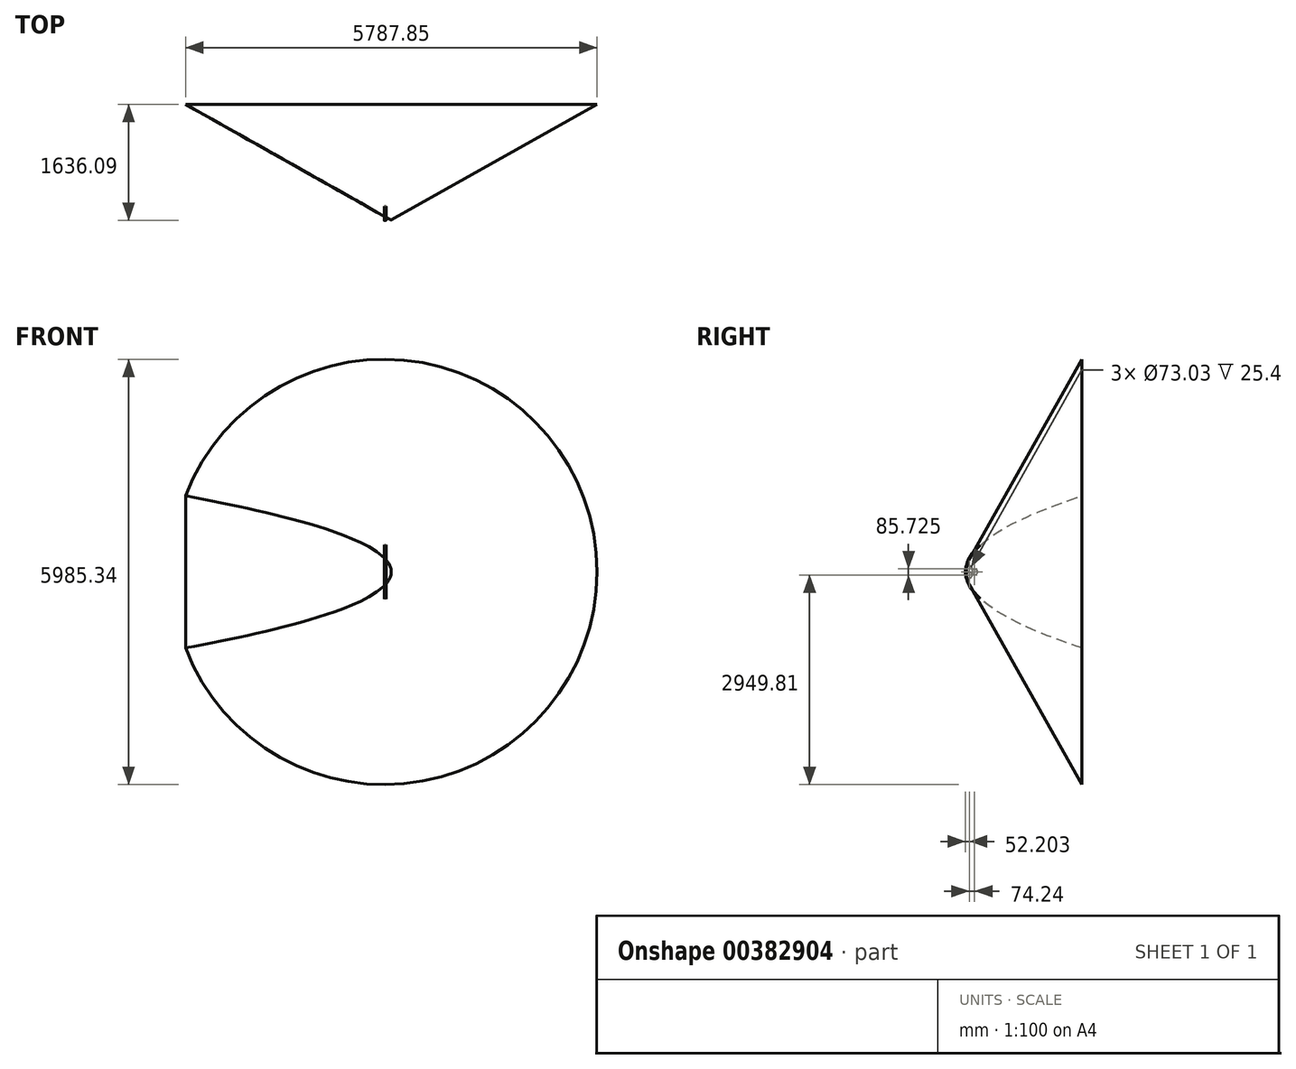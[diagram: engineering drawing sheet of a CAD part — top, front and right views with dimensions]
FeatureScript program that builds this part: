
annotation { "Feature Type Name" : "Feature", "Feature Type Description" : "" }
export const myFeature = defineFeature(function(context is Context, id is Id, definition is map)
    precondition{}
    {
        {
            var Q0;
            Q0=qCreatedBy(makeId("Top.planeOp"),FACE);
            var sketch = newSketch(context, id + "F0", { "sketchPlane" : qUnion([Q0])});
            skLineSegment(sketch, "E0", {"start": v(0, 0) * mm, "end": v(2992.67, 1685.34) * mm});
            skLineSegment(sketch, "E1", {"start": v(2992.67, 1685.34) * mm, "end": v(0, 1685.34) * mm});
            skLineSegment(sketch, "E2", {"start": v(0, 1685.34) * mm, "end": v(0, 0) * mm});
            skSolve(sketch);
        }
        {
            var Q0;
            Q0=makeQuery(id+"F0.imprint","IMPRINT",FACE,{"disambiguationData":[TD([[makeQuery(id+"F0.imprint","IMPRINT",EDGE,{"derivedFrom":sQuery(id+"F0.wireOp",EDGE,"E0")}),1.0]])]});
            var Q1;
            Q1=sQuery(id+"F0.wireOp",EDGE,"E2");
            revolve(context, id + "F1", {"entities" : qUnion([Q0]), "axis" : qUnion([Q1]), "revolveType" : RevolveType.FULL});
        }
        {
            var Q0;
            Q0=qCreatedBy(makeId("Top.planeOp"),FACE);
            var sketch = newSketch(context, id + "F2", { "sketchPlane" : qUnion([Q0])});
            skLineSegment(sketch, "E3", {"start": v(0, 0) * mm, "end": v(-231.31, 130.27) * mm, "construction": true});
            skLineSegment(sketch, "E4.0", {"start": v(398.44, -113.17) * mm, "end": v(151.52, 25.89) * mm});
            skLineSegment(sketch, "E5", {"start": v(398.44, -113.17) * mm, "end": v(601.1, -227.3) * mm});
            skLineSegment(sketch, "E6", {"start": v(601.1, -227.3) * mm, "end": v(-3246.67, -227.3) * mm});
            skLineSegment(sketch, "E7", {"start": v(-3246.67, -227.3) * mm, "end": v(-3246.67, 1939.6) * mm});
            skLineSegment(sketch, "E8", {"start": v(151.52, 25.89) * mm, "end": v(-3246.67, 1939.6) * mm});
            skLineSegment(sketch, "E9.0", {"start": v(-2992.67, 1685.34) * mm, "end": v(2992.67, 1685.34) * mm, "construction": true});
            skSolve(sketch);
        }
        {
            var Q0;
            Q0 = qSketchRegion(id + "F2", true);
            extrude(context, id + "F3", {"entities" : qUnion([Q0]), "operationType" : NewBodyOperationType.REMOVE, "endBound" : BoundingType.THROUGH_ALL, "oppositeDirection" : true, "depth" : 25.4 * mm, "hasSecondDirection" : true, "secondDirectionBound" : BoundingType.THROUGH_ALL, "secondDirectionOppositeDirection" : false, "secondDirectionDepth" : 25.4 * mm});
        }
        {
            var Q0;
            Q0=qCreatedBy(makeId("Right.planeOp"),FACE);
            var sketch = newSketch(context, id + "F4", { "sketchPlane" : qUnion([Q0])});
            skLineSegment(sketch, "E10", {"start": v(230.95, -350.68) * mm, "end": v(581.64, 0) * mm, "construction": true});
            skLineSegment(sketch, "E11", {"start": v(581.64, 0) * mm, "end": v(230.95, 350.68) * mm, "construction": true});
            skPoint(sketch, "E12", {"position": v(55.6, 0) * mm});
            skCircle(sketch, "E13", {"center": v(175.7, 0) * mm, "radius": 42.86 * mm});
            skCircle(sketch, "E14", {"center": v(101.45, 42.86) * mm, "radius": 42.86 * mm});
            skCircle(sketch, "E15", {"center": v(101.45, -42.86) * mm, "radius": 42.86 * mm});
            skLineSegment(sketch, "E16", {"start": v(230.95, -350.68) * mm, "end": v(230.95, 350.68) * mm, "construction": true});
            skPoint(sketch, "E17", {"position": v(218.56, 0) * mm});
            skLineSegment(sketch, "E18", {"start": v(55.6, 0) * mm, "end": v(55.6, -375.44) * mm, "construction": true});
            skLineSegment(sketch, "E19", {"start": v(55.6, 0) * mm, "end": v(55.6, 375.44) * mm, "construction": true});
            skLineSegment(sketch, "E20", {"start": v(55.6, -375.44) * mm, "end": v(256.58, -375.44) * mm, "construction": true});
            skLineSegment(sketch, "E21", {"start": v(55.6, 375.44) * mm, "end": v(256.58, 375.44) * mm, "construction": true});
            skFitSpline(sketch, "E22", {"points": [v(1685.34, 1069.12) * mm, v(1649.33, 1057.31) * mm, v(1577.35, 1033.3) * mm, v(1469.49, 996.05) * mm, v(1361.76, 957.39) * mm, v(1254.16, 917.16) * mm, v(1146.74, 875.15) * mm, v(1057.36, 838.44) * mm, v(985.98, 807.9) * mm, v(932.5, 784.34) * mm, v(879.08, 760.1) * mm, v(825.77, 735.1) * mm, v(772.56, 709.27) * mm, v(719.47, 682.53) * mm, v(666.5, 654.77) * mm, v(622.48, 630.67) * mm, v(587.34, 610.75) * mm, v(561.03, 595.45) * mm, v(534.77, 579.78) * mm, v(499.82, 558.35) * mm, v(456.36, 530.53) * mm, v(404.61, 495.2) * mm, v(361.9, 463.81) * mm, v(328.04, 437.27) * mm, v(302.8, 416.56) * mm, v(277.77, 394.94) * mm, v(252.95, 372.28) * mm, v(228.4, 348.4) * mm, v(204.13, 323.1) * mm, v(184.22, 300.6) * mm, v(168.5, 281.52) * mm, v(156.85, 266.62) * mm, v(147.26, 253.64) * mm, v(139.67, 242.86) * mm, v(134.96, 235.94) * mm, v(131.22, 230.3) * mm, v(128.43, 226) * mm, v(125.65, 221.66) * mm, v(121.98, 215.8) * mm, v(117.45, 208.33) * mm, v(110.35, 196.1) * mm, v(103.46, 183.4) * mm, v(96.83, 170.14) * mm, v(92, 159.88) * mm, v(88.11, 151.06) * mm, v(85.08, 143.82) * mm, v(82.86, 138.28) * mm, v(80.68, 132.65) * mm, v(78.57, 126.95) * mm, v(76.52, 121.17) * mm, v(73.89, 113.34) * mm, v(70.77, 103.35) * mm, v(67.9, 93.03) * mm, v(65.79, 84.57) * mm, v(64.29, 78.12) * mm, v(63.12, 72.64) * mm, v(62.23, 68.2) * mm, v(61.39, 63.74) * mm, v(60.4, 58.13) * mm, v(59, 49.08) * mm, v(57.83, 39.9) * mm, v(56.92, 30.62) * mm, v(56.38, 23.59) * mm, v(56.04, 17.67) * mm, v(55.84, 12.9) * mm, v(55.73, 9.31) * mm, v(55.65, 5.72) * mm, v(55.6, 0.94) * mm, v(55.62, -5) * mm, v(55.8, -12.1) * mm, v(56.21, -21.53) * mm, v(56.91, -30.88) * mm, v(57.89, -40.17) * mm, v(58.6, -45.94) * mm, v(59.24, -50.54) * mm, v(59.93, -55.14) * mm, v(60.86, -60.8) * mm, v(62.08, -67.48) * mm, v(63.85, -76.25) * mm, v(66.31, -86.95) * mm, v(69.08, -97.35) * mm, v(71.46, -105.49) * mm, v(73.32, -111.52) * mm, v(75.26, -117.46) * mm, v(77.28, -123.34) * mm, v(79.36, -129.1) * mm, v(82.2, -136.64) * mm, v(85.86, -145.8) * mm, v(90.45, -156.45) * mm, v(96.8, -170.2) * mm, v(103.43, -183.33) * mm, v(110.32, -195.96) * mm, v(115.6, -205.2) * mm, v(121, -214.22) * mm, v(126.5, -223.04) * mm, v(132.06, -231.6) * mm, v(139.54, -242.74) * mm, v(149.04, -256.14) * mm, v(160.62, -271.52) * mm, v(176.27, -291.19) * mm, v(196.2, -314.4) * mm, v(220.58, -340.47) * mm, v(245.35, -365.06) * mm, v(266.27, -384.5) * mm, v(283.14, -399.53) * mm, v(295.86, -410.54) * mm, v(308.64, -421.31) * mm, v(325.76, -435.39) * mm, v(347.24, -452.4) * mm, v(373.1, -472.02) * mm, v(399.06, -490.91) * mm, v(425.1, -509.16) * mm, v(459.9, -532.72) * mm, v(503.58, -560.85) * mm, v(556.22, -592.81) * mm, v(609.04, -623.26) * mm, v(662.03, -652.37) * mm, v(715.16, -680.32) * mm, v(768.42, -707.23) * mm, v(839.6, -741.86) * mm, v(928.81, -783.07) * mm, v(1036.22, -829.73) * mm, v(1143.93, -874.02) * mm, v(1251.88, -916.29) * mm, v(1360.06, -956.77) * mm, v(1468.37, -995.66) * mm, v(1576.8, -1033.12) * mm, v(1649.15, -1057.25) * mm, v(1685.34, -1069.12) * mm]});
            skFitSpline(sketch, "E23.0", {"points": [v(252.25, 380.08) * mm, v(241.58, 370.12) * mm, v(225.68, 354.67) * mm, v(204.71, 332.85) * mm, v(189.13, 315.79) * mm, v(173.7, 297.93) * mm, v(158.45, 279.16) * mm, v(145.92, 262.63) * mm, v(136.03, 248.77) * mm, v(129.9, 239.81) * mm, v(125.04, 232.46) * mm, v(121.4, 226.83) * mm, v(117.82, 221.13) * mm, v(113.09, 213.4) * mm, v(107.27, 203.52) * mm, v(100.47, 191.26) * mm, v(93.87, 178.56) * mm, v(88.56, 167.56) * mm, v(84.44, 158.48) * mm, v(81.41, 151.52) * mm, v(78.46, 144.4) * mm, v(75.58, 137.12) * mm, v(72.8, 129.7) * mm, v(70.13, 122.13) * mm, v(67.57, 114.43) * mm, v(65.14, 106.57) * mm, v(62.83, 98.55) * mm, v(60.66, 90.36) * mm, v(58.64, 82) * mm, v(57.09, 74.86) * mm, v(55.93, 69.04) * mm, v(55.1, 64.66) * mm, v(54.33, 60.25) * mm, v(53.37, 54.34) * mm, v(52.3, 46.9) * mm, v(51.23, 37.85) * mm, v(50.51, 30.23) * mm, v(50.06, 24.08) * mm, v(49.78, 19.44) * mm, v(49.55, 14.77) * mm, v(49.39, 10.07) * mm, v(49.29, 5.35) * mm, v(49.25, 0.66) * mm, v(49.27, -4.01) * mm, v(49.38, -10.23) * mm, v(49.67, -17.96) * mm, v(50.25, -27.17) * mm, v(50.93, -34.8) * mm, v(51.59, -40.88) * mm, v(52.14, -45.42) * mm, v(52.74, -49.95) * mm, v(53.4, -54.46) * mm, v(54.11, -58.93) * mm, v(55.12, -64.82) * mm, v(56.5, -72.07) * mm, v(58.32, -80.6) * mm, v(60.3, -88.94) * mm, v(62.44, -97.13) * mm, v(64.73, -105.17) * mm, v(67.14, -113.07) * mm, v(69.26, -119.54) * mm, v(71.02, -124.66) * mm, v(72.82, -129.7) * mm, v(75.11, -135.9) * mm, v(77.95, -143.16) * mm, v(81.85, -152.62) * mm, v(86.9, -164.06) * mm, v(93.22, -177.25) * mm, v(99.78, -189.96) * mm, v(106.54, -202.24) * mm, v(112.34, -212.15) * mm, v(117.06, -219.9) * mm, v(121.83, -227.53) * mm, v(127.86, -236.8) * mm, v(135.19, -247.56) * mm, v(142.6, -257.99) * mm, v(150.08, -268.1) * mm, v(160.15, -281.23) * mm, v(172.9, -296.98) * mm, v(188.43, -315) * mm, v(204.14, -332.24) * mm, v(225.32, -354.32) * mm, v(241.43, -369.97) * mm, v(252.25, -380.08) * mm]});
            skLineSegment(sketch, "E24", {"start": v(256.58, -375.44) * mm, "end": v(252.25, -380.08) * mm});
            skLineSegment(sketch, "E25", {"start": v(256.58, 375.44) * mm, "end": v(252.25, 380.08) * mm});
            skCircle(sketch, "E26.0", {"center": v(175.7, 0) * mm, "radius": 36.51 * mm});
            skCircle(sketch, "E27.0", {"center": v(101.45, 42.86) * mm, "radius": 36.51 * mm});
            skCircle(sketch, "E28.0", {"center": v(101.45, -42.86) * mm, "radius": 36.51 * mm});
            skSolve(sketch);
        }
        {
            var Q0;
            Q0=makeQuery(id+"F4.imprint","IMPRINT",FACE,{"disambiguationData":[TD([[makeQuery(id+"F4.imprint","IMPRINT",EDGE,{"derivedFrom":sQuery(id+"F4.wireOp",EDGE,"E23.0")}),1.0]])]});
            var Q1;
            Q1=makeQuery(id+"F4.imprint","IMPRINT",FACE,{"disambiguationData":[TD([[makeQuery(id+"F4.imprint","IMPRINT",EDGE,{"derivedFrom":sQuery(id+"F4.wireOp",EDGE,"E28.0")}),-1.0]])]});
            var Q2;
            Q2=makeQuery(id+"F4.imprint","IMPRINT",FACE,{"disambiguationData":[TD([[makeQuery(id+"F4.imprint","IMPRINT",EDGE,{"derivedFrom":sQuery(id+"F4.wireOp",EDGE,"E27.0")}),-1.0]])]});
            var Q3;
            Q3=makeQuery(id+"F4.imprint","IMPRINT",FACE,{"disambiguationData":[TD([[makeQuery(id+"F4.imprint","IMPRINT",EDGE,{"derivedFrom":sQuery(id+"F4.wireOp",EDGE,"E26.0")}),-1.0]])]});
            var Q4;
            {var subQ0=sQuery(id+"F4.wireOp",EDGE,"E14");var subQ1=sQuery(id+"F4.wireOp",EDGE,"E13");var subQ2=makeQuery(id+"F4.imprint","INTERSECT",VERTEX,{"derivedFrom":[subQ1,subQ0]});Q4=makeQuery(id+"F4.imprint","IMPRINT",FACE,{"disambiguationData":[TD([[makeQuery(id+"F4.imprint","IMPRINT",EDGE,{"disambiguationData":[TD([[subQ2,-1.0]])],"derivedFrom":subQ1}),-1.0]])]});}
            var Q5;
            {var subQ0=sQuery(id+"F4.wireOp",EDGE,"E22");var subQ1=sQuery(id+"F4.wireOp",EDGE,"E14");var subQ2=makeQuery(id+"F4.imprint","INTERSECT",VERTEX,{"derivedFrom":[subQ1,subQ0]});Q5=makeQuery(id+"F4.imprint","IMPRINT",FACE,{"disambiguationData":[TD([[makeQuery(id+"F4.imprint","IMPRINT",EDGE,{"disambiguationData":[TD([[subQ2,-1.0]])],"derivedFrom":subQ1}),-1.0]])]});}
            extrude(context, id + "F5", {"entities" : qUnion([Q0, Q1, Q2, Q3, Q4, Q5]), "depth" : 25.4 * mm});
        }
    });
